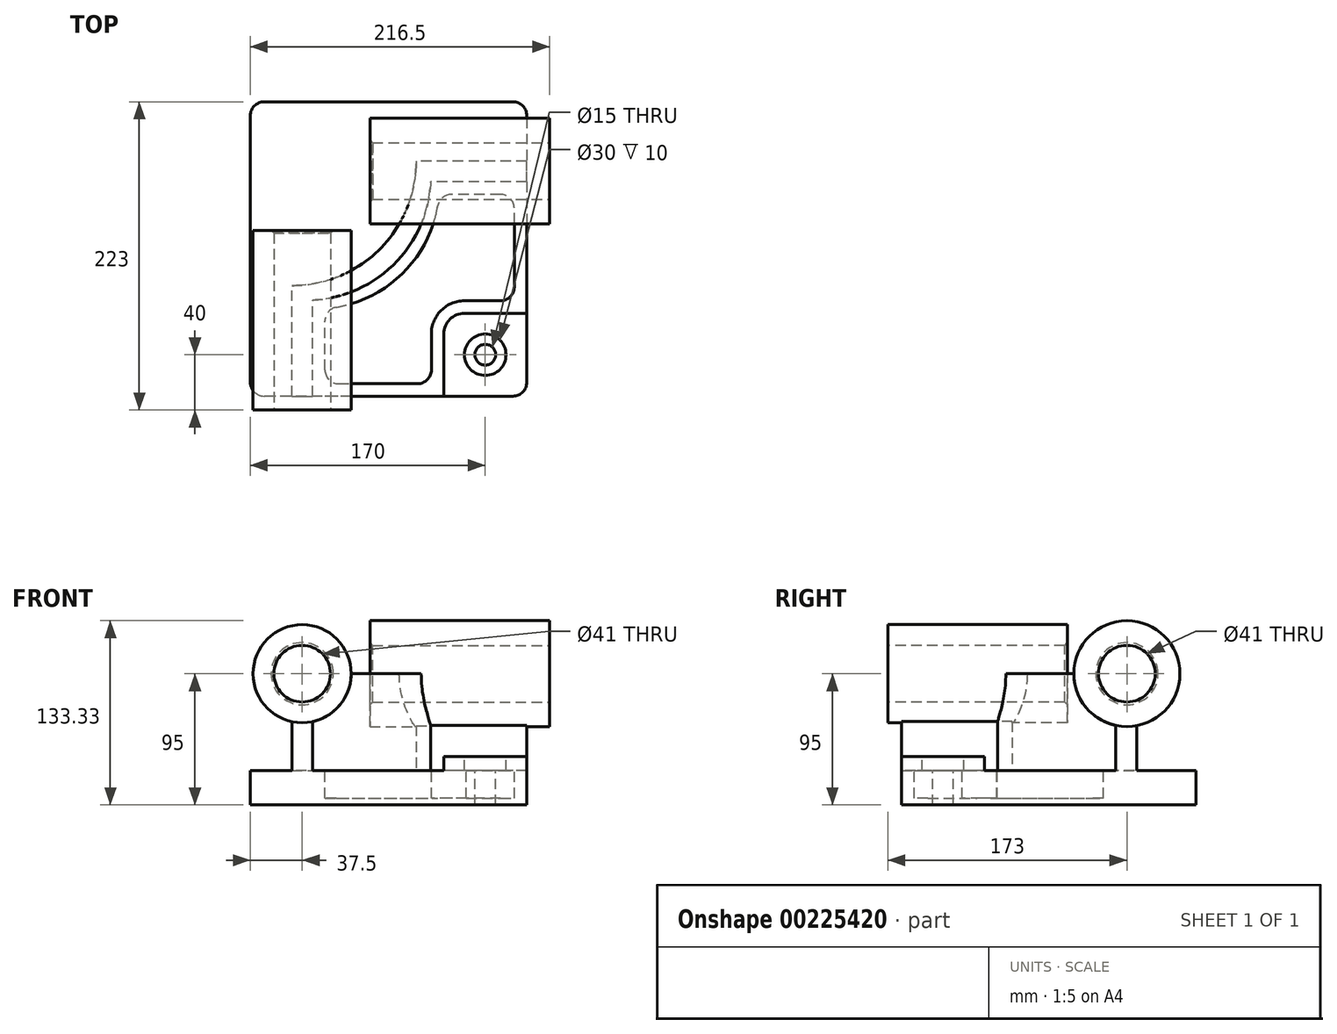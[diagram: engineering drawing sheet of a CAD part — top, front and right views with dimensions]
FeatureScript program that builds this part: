
annotation { "Feature Type Name" : "Feature", "Feature Type Description" : "" }
export const myFeature = defineFeature(function(context is Context, id is Id, definition is map)
    precondition{}
    {
        {
            var Q0;
            Q0=qCreatedBy(makeId("Top.planeOp"),FACE);
            var sketch = newSketch(context, id + "F0", { "sketchPlane" : qUnion([Q0])});
            skLineSegment(sketch, "E0.bottom", {"start": v(100, 106.5) * mm, "end": v(-100, 106.5) * mm});
            skLineSegment(sketch, "E0.top", {"start": v(100, -106.5) * mm, "end": v(-100, -106.5) * mm});
            skLineSegment(sketch, "E0.left", {"start": v(100, 106.5) * mm, "end": v(100, -106.5) * mm});
            skLineSegment(sketch, "E0.right", {"start": v(-100, 106.5) * mm, "end": v(-100, -106.5) * mm});
            skPoint(sketch, "E0.middle", {"position": v(0, 0) * mm});
            skSolve(sketch);
        }
        {
            var Q0;
            Q0 = qSketchRegion(id + "F0", true);
            extrude(context, id + "F1", {"entities" : qUnion([Q0]), "depth" : 25 * mm});
        }
        {
            var Q0;
            Q0=makeQuery(id+"F1.opExtrude","CAP_FACE",FACE,{"disambiguationData":[OSD([sQuery(id+"F0.wireOp",EDGE,"E0.bottom"),sQuery(id+"F0.wireOp",EDGE,"E0.top"),sQuery(id+"F0.wireOp",EDGE,"E0.left"),sQuery(id+"F0.wireOp",EDGE,"E0.right")])],"isStart":false});
            var sketch = newSketch(context, id + "F2", { "sketchPlane" : qUnion([Q0])});
            skLineSegment(sketch, "E1.bottom", {"start": v(-70, -106.5) * mm, "end": v(-55, -106.5) * mm});
            skLineSegment(sketch, "E1.left", {"start": v(-70, -106.5) * mm, "end": v(-70, -26.5) * mm});
            skLineSegment(sketch, "E1.right", {"start": v(-55, -106.5) * mm, "end": v(-55, -37) * mm});
            skLineSegment(sketch, "E2.bottom", {"start": v(100, 63.5) * mm, "end": v(20, 63.5) * mm});
            skLineSegment(sketch, "E2.top", {"start": v(100, 48.5) * mm, "end": v(30.5, 48.5) * mm});
            skLineSegment(sketch, "E2.left", {"start": v(100, 63.5) * mm, "end": v(100, 48.5) * mm});
            skArc(sketch, "E3", {"start": v(-70, -26.5) * mm, "mid": v(-6.36, -0.14) * mm, "end": v(20, 63.5) * mm});
            skArc(sketch, "E4", {"start": v(-55, -37) * mm, "mid": v(4.25, -10.75) * mm, "end": v(30.5, 48.5) * mm});
            skSolve(sketch);
        }
        {
            var Q0;
            Q0 = qSketchRegion(id + "F2", true);
            extrude(context, id + "F3", {"entities" : qUnion([Q0]), "operationType" : NewBodyOperationType.ADD, "depth" : 70 * mm});
        }
        {
            var Q0;
            Q0=qCreatedBy(makeId("Front.planeOp"),FACE);
            cPlane(context, id + "F4", {"entities" : qUnion([Q0]), "cplaneType" : CPlaneType.OFFSET, "offset" : 116.5 * mm, "width" : 150 * mm, "height" : 150 * mm});
        }
        {
            var Q0;
            Q0=qCreatedBy(id+"F4.planeOp",FACE);
            var sketch = newSketch(context, id + "F5", { "sketchPlane" : qUnion([Q0])});
            skCircle(sketch, "E5", {"center": v(-62.5, 95) * mm, "radius": 35.5 * mm});
            skSolve(sketch);
        }
        {
            var Q0;
            Q0 = qSketchRegion(id + "F5", true);
            extrude(context, id + "F6", {"entities" : qUnion([Q0]), "operationType" : NewBodyOperationType.ADD, "oppositeDirection" : true, "depth" : 130 * mm});
        }
        {
            var Q0;
            Q0=qCreatedBy(makeId("Right.planeOp"),FACE);
            cPlane(context, id + "F7", {"entities" : qUnion([Q0]), "cplaneType" : CPlaneType.OFFSET, "offset" : 116.5 * mm, "width" : 150 * mm, "height" : 150 * mm});
        }
        {
            var Q0;
            Q0=qCreatedBy(id+"F7.planeOp",FACE);
            var sketch = newSketch(context, id + "F8", { "sketchPlane" : qUnion([Q0])});
            skCircle(sketch, "E6", {"center": v(56.5, 95) * mm, "radius": 38.33 * mm});
            skSolve(sketch);
        }
        {
            var Q0;
            Q0 = qSketchRegion(id + "F8", true);
            extrude(context, id + "F9", {"entities" : qUnion([Q0]), "operationType" : NewBodyOperationType.ADD, "oppositeDirection" : true, "depth" : 130 * mm});
        }
        {
            var Q0;
            Q0=makeQuery(id+"F9.opExtrude","CAP_FACE",FACE,{"disambiguationData":[OSD([sQuery(id+"F8.wireOp",EDGE,"E6")])],"isStart":true});
            var sketch = newSketch(context, id + "F10", { "sketchPlane" : qUnion([Q0])});
            skCircle(sketch, "E7", {"center": v(56.5, 95) * mm, "radius": 20.5 * mm});
            skSolve(sketch);
        }
        {
            var Q0;
            Q0 = qSketchRegion(id + "F10", true);
            extrude(context, id + "F11", {"entities" : qUnion([Q0]), "operationType" : NewBodyOperationType.REMOVE, "endBound" : BoundingType.THROUGH_ALL, "oppositeDirection" : true, "depth" : 25 * mm});
        }
        {
            var Q0;
            Q0=makeQuery(id+"F6.opExtrude","CAP_FACE",FACE,{"disambiguationData":[OSD([sQuery(id+"F5.wireOp",EDGE,"E5")])],"isStart":true});
            var sketch = newSketch(context, id + "F12", { "sketchPlane" : qUnion([Q0])});
            skCircle(sketch, "E8", {"center": v(-62.5, 95) * mm, "radius": 20.5 * mm});
            skSolve(sketch);
        }
        {
            var Q0;
            Q0=makeQuery(id+"F12.imprint","IMPRINT",FACE,{"disambiguationData":[TD([[makeQuery(id+"F12.imprint","IMPRINT",EDGE,{"derivedFrom":sQuery(id+"F12.wireOp",EDGE,"E8")}),1.0]])]});
            var Q1;
            Q1=sQuery(id+"F12.wireOp",EDGE,"E8");
            extrude(context, id + "F13", {"entities" : qUnion([Q0]), "operationType" : NewBodyOperationType.REMOVE, "surfaceEntities" : qUnion([Q1]), "endBound" : BoundingType.THROUGH_ALL, "oppositeDirection" : true, "depth" : 25 * mm});
        }
        {
            var Q0;
            {var subQ0=sQuery(id+"F0.wireOp",EDGE,"E0.left");var subQ1=sQuery(id+"F0.wireOp",EDGE,"E0.top");Q0=makeQuery(id+"F3.boolean.opBoolean","SPLIT",FACE,{"disambiguationData":[TD([makeQuery(id+"F3.opExtrude","SWEPT_FACE",FACE,{"disambiguationData":[OSD([sQuery(id+"F2.wireOp",EDGE,"E1.right")])]})])],"derivedFrom":makeQuery(id+"F1.opExtrude","CAP_FACE",FACE,{"disambiguationData":[OSD([sQuery(id+"F0.wireOp",EDGE,"E0.bottom"),subQ1,subQ0,sQuery(id+"F0.wireOp",EDGE,"E0.right")])],"isStart":false})});}
            var sketch = newSketch(context, id + "F14", { "sketchPlane" : qUnion([Q0])});
            skLineSegment(sketch, "E9.bottom", {"start": v(100, -106.5) * mm, "end": v(40, -106.5) * mm});
            skLineSegment(sketch, "E9.top", {"start": v(100, -46.5) * mm, "end": v(40, -46.5) * mm});
            skLineSegment(sketch, "E9.left", {"start": v(100, -106.5) * mm, "end": v(100, -46.5) * mm});
            skLineSegment(sketch, "E9.right", {"start": v(40, -106.5) * mm, "end": v(40, -46.5) * mm});
            skSolve(sketch);
        }
        {
            var Q0;
            Q0 = qSketchRegion(id + "F14", true);
            extrude(context, id + "F15", {"entities" : qUnion([Q0]), "operationType" : NewBodyOperationType.ADD, "depth" : 10 * mm});
        }
        {
            var Q0;
            Q0=makeQuery(id+"F15.opExtrude","CAP_FACE",FACE,{"disambiguationData":[OSD([sQuery(id+"F14.wireOp",EDGE,"E9.bottom"),sQuery(id+"F14.wireOp",EDGE,"E9.top"),sQuery(id+"F14.wireOp",EDGE,"E9.left"),sQuery(id+"F14.wireOp",EDGE,"E9.right")])],"isStart":false});
            var sketch = newSketch(context, id + "F16", { "sketchPlane" : qUnion([Q0])});
            skPoint(sketch, "E10", {"position": v(70, -76.5) * mm});
            skSolve(sketch);
        }
        {
            var Q0;
            Q0=sQuery(id+"F16.wireOp",VERTEX,"E10");
            var Q1;
            Q1=makeQuery(id+"F1.opExtrude","SWEPT_BODY",BODY,{"disambiguationData":[OSD([sQuery(id+"F0.wireOp",EDGE,"E0.bottom"),sQuery(id+"F0.wireOp",EDGE,"E0.top"),sQuery(id+"F0.wireOp",EDGE,"E0.left"),sQuery(id+"F0.wireOp",EDGE,"E0.right")])]});
            hole(context, id + "F17", {"style" : HoleStyle.C_BORE, "endStyle" : HoleEndStyle.THROUGH, "holeDiameter" : 15 * mm, "cBoreDiameter" : 30 * mm, "cBoreDepth" : 10 * mm, "locations" : qUnion([Q0]), "scope" : qUnion([Q1]), "isTappedThrough" : true});
        }
        {
            var Q0;
            Q0=makeQuery(id+"F1.opExtrude","SWEPT_EDGE",EDGE,{"disambiguationData":[OSD([sQuery(id+"F0.wireOp",EDGE,"E0.bottom"),sQuery(id+"F0.wireOp",EDGE,"E0.left")])]});
            var Q1;
            Q1=makeQuery(id+"F15.boolean.opBoolean","MERGE",EDGE,{"derivedFrom":[makeQuery(id+"F1.opExtrude","SWEPT_EDGE",EDGE,{"disambiguationData":[OSD([sQuery(id+"F0.wireOp",EDGE,"E0.top"),sQuery(id+"F0.wireOp",EDGE,"E0.left")])]}),makeQuery(id+"F15.opExtrude","SWEPT_EDGE",EDGE,{"disambiguationData":[OSD([sQuery(id+"F14.wireOp",EDGE,"E9.bottom"),sQuery(id+"F14.wireOp",EDGE,"E9.left")])]})]});
            var Q2;
            Q2=makeQuery(id+"F1.opExtrude","SWEPT_EDGE",EDGE,{"disambiguationData":[OSD([sQuery(id+"F0.wireOp",EDGE,"E0.top"),sQuery(id+"F0.wireOp",EDGE,"E0.right")])]});
            var Q3;
            Q3=makeQuery(id+"F1.opExtrude","SWEPT_EDGE",EDGE,{"disambiguationData":[OSD([sQuery(id+"F0.wireOp",EDGE,"E0.bottom"),sQuery(id+"F0.wireOp",EDGE,"E0.right")])]});
            fillet(context, id + "F18", {"entities" : qUnion([Q0, Q1, Q2, Q3]), "radius" : 10 * mm, "tangentPropagation" : true, "allowEdgeOverflow" : false});
        }
        {
            var Q0;
            Q0=makeQuery(id+"F15.opExtrude","SWEPT_EDGE",EDGE,{"disambiguationData":[OSD([sQuery(id+"F14.wireOp",EDGE,"E9.top"),sQuery(id+"F14.wireOp",EDGE,"E9.right")])]});
            fillet(context, id + "F19", {"entities" : qUnion([Q0]), "radius" : 15 * mm, "tangentPropagation" : true, "allowEdgeOverflow" : false});
        }
        {
            var Q0;
            {var subQ0=sQuery(id+"F0.wireOp",EDGE,"E0.left");var subQ1=sQuery(id+"F0.wireOp",EDGE,"E0.top");Q0=makeQuery(id+"F3.boolean.opBoolean","SPLIT",FACE,{"disambiguationData":[TD([makeQuery(id+"F3.opExtrude","SWEPT_FACE",FACE,{"disambiguationData":[OSD([sQuery(id+"F2.wireOp",EDGE,"E1.right")])]})])],"derivedFrom":makeQuery(id+"F1.opExtrude","CAP_FACE",FACE,{"disambiguationData":[OSD([sQuery(id+"F0.wireOp",EDGE,"E0.bottom"),subQ1,subQ0,sQuery(id+"F0.wireOp",EDGE,"E0.right")])],"isStart":false})});}
            var sketch = newSketch(context, id + "F20", { "sketchPlane" : qUnion([Q0])});
            skLineSegment(sketch, "E11", {"start": v(-46, -97.5) * mm, "end": v(31, -97.5) * mm});
            skLineSegment(sketch, "E12", {"start": v(31, -97.5) * mm, "end": v(31, -62.76) * mm});
            skLineSegment(sketch, "E13", {"start": v(56.26, -37.5) * mm, "end": v(91, -37.5) * mm});
            skLineSegment(sketch, "E14", {"start": v(91, -37.5) * mm, "end": v(91, 39.5) * mm});
            skArc(sketch, "E15", {"start": v(-46, -43.2) * mm, "mid": v(10.61, -17.11) * mm, "end": v(36.7, 39.5) * mm});
            skLineSegment(sketch, "E16", {"start": v(-46, -97.5) * mm, "end": v(-46, -43.2) * mm});
            skLineSegment(sketch, "E17", {"start": v(91, 39.5) * mm, "end": v(36.7, 39.5) * mm});
            skPoint(sketch, "E18.orphan", {"position": v(4.25, -10.75) * mm});
            skPoint(sketch, "E19.end.orphan", {"position": v(-59.4, 52.9) * mm});
            skArc(sketch, "E20", {"start": v(56.26, -37.5) * mm, "mid": v(38, -44.5) * mm, "end": v(31, -62.76) * mm});
            skPoint(sketch, "E21.start.orphan", {"position": v(44.4, -50.9) * mm});
            skSolve(sketch);
        }
        {
            var Q0;
            Q0 = qSketchRegion(id + "F20", true);
            extrude(context, id + "F21", {"entities" : qUnion([Q0]), "operationType" : NewBodyOperationType.REMOVE, "oppositeDirection" : true, "depth" : 20 * mm});
        }
        {
            var Q0;
            Q0=makeQuery(id+"F21.boolean.opBoolean","COPY",EDGE,{"derivedFrom":makeQuery(id+"F21.opExtrude","SWEPT_EDGE",EDGE,{"disambiguationData":[OSD([sQuery(id+"F20.wireOp",EDGE,"E15"),sQuery(id+"F20.wireOp",EDGE,"E17")])]})});
            var Q1;
            Q1=makeQuery(id+"F21.boolean.opBoolean","COPY",EDGE,{"derivedFrom":makeQuery(id+"F21.opExtrude","SWEPT_EDGE",EDGE,{"disambiguationData":[OSD([sQuery(id+"F20.wireOp",EDGE,"E15"),sQuery(id+"F20.wireOp",EDGE,"E16")])]})});
            var Q2;
            Q2=makeQuery(id+"F21.boolean.opBoolean","COPY",EDGE,{"derivedFrom":makeQuery(id+"F21.opExtrude","SWEPT_EDGE",EDGE,{"disambiguationData":[OSD([sQuery(id+"F20.wireOp",EDGE,"E14"),sQuery(id+"F20.wireOp",EDGE,"E17")])]})});
            var Q3;
            Q3=makeQuery(id+"F21.boolean.opBoolean","COPY",EDGE,{"derivedFrom":makeQuery(id+"F21.opExtrude","SWEPT_EDGE",EDGE,{"disambiguationData":[OSD([sQuery(id+"F20.wireOp",EDGE,"E13"),sQuery(id+"F20.wireOp",EDGE,"E14")])]})});
            var Q4;
            Q4=makeQuery(id+"F21.boolean.opBoolean","COPY",EDGE,{"derivedFrom":makeQuery(id+"F21.opExtrude","SWEPT_EDGE",EDGE,{"disambiguationData":[OSD([sQuery(id+"F20.wireOp",EDGE,"E11"),sQuery(id+"F20.wireOp",EDGE,"E12")])]})});
            var Q5;
            Q5=makeQuery(id+"F21.boolean.opBoolean","COPY",EDGE,{"derivedFrom":makeQuery(id+"F21.opExtrude","SWEPT_EDGE",EDGE,{"disambiguationData":[OSD([sQuery(id+"F20.wireOp",EDGE,"E11"),sQuery(id+"F20.wireOp",EDGE,"E16")])]})});
            fillet(context, id + "F22", {"entities" : qUnion([Q0, Q1, Q2, Q3, Q4, Q5]), "radius" : 10 * mm, "tangentPropagation" : true, "allowEdgeOverflow" : false});
        }
        {
            var Q0;
            Q0=makeQuery(id+"F13.boolean.opBoolean","COPY",EDGE,{"derivedFrom":makeQuery(id+"F13.opExtrude","CAP_EDGE",EDGE,{"disambiguationData":[OSD([sQuery(id+"F12.wireOp",EDGE,"E8")])],"isStart":true})});
            var Q1;
            Q1=makeQuery(id+"F11.boolean.opBoolean","COPY",EDGE,{"derivedFrom":makeQuery(id+"F11.opExtrude","CAP_EDGE",EDGE,{"disambiguationData":[OSD([sQuery(id+"F10.wireOp",EDGE,"E7")])],"isStart":true})});
            var Q2;
            Q2=makeQuery(id+"F11.boolean.opBoolean","INTERSECT",EDGE,{"derivedFrom":[makeQuery(id+"F9.opExtrude","CAP_FACE",FACE,{"disambiguationData":[OSD([sQuery(id+"F8.wireOp",EDGE,"E6")])],"isStart":false}),makeQuery(id+"F11.opExtrude","SWEPT_FACE",FACE,{"disambiguationData":[OSD([sQuery(id+"F10.wireOp",EDGE,"E7")])]})]});
            var Q3;
            Q3=makeQuery(id+"F13.boolean.opBoolean","INTERSECT",EDGE,{"derivedFrom":[makeQuery(id+"F6.opExtrude","CAP_FACE",FACE,{"disambiguationData":[OSD([sQuery(id+"F5.wireOp",EDGE,"E5")])],"isStart":false}),makeQuery(id+"F13.opExtrude","SWEPT_FACE",FACE,{"disambiguationData":[OSD([sQuery(id+"F12.wireOp",EDGE,"E8")])]})]});
            chamfer(context, id + "F23", {"entities" : qUnion([Q0, Q1, Q2, Q3]), "chamferType" : ChamferType.OFFSET_ANGLE, "width" : 2 * mm, "oppositeDirection" : false, "angle" : 45 * degree, "tangentPropagation" : true});
        }
    });
